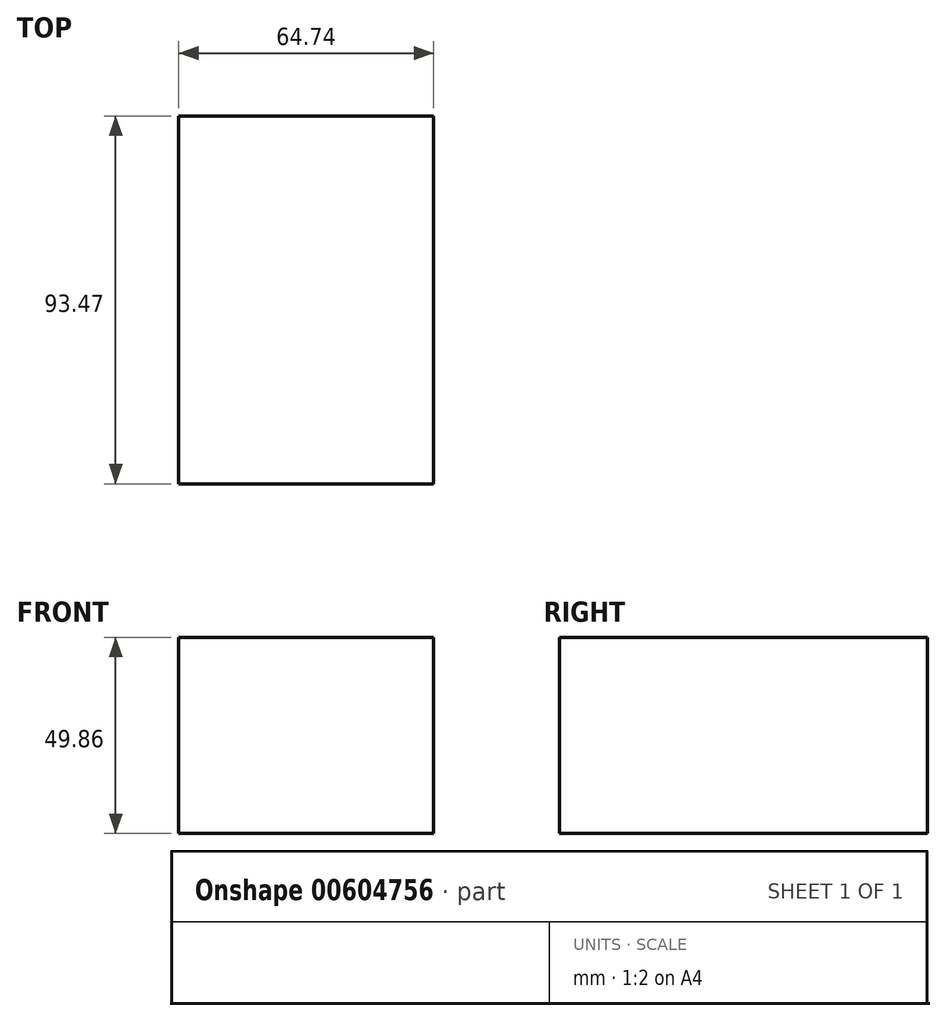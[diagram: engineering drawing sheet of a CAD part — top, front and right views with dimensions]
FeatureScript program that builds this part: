
annotation { "Feature Type Name" : "Feature", "Feature Type Description" : "" }
export const myFeature = defineFeature(function(context is Context, id is Id, definition is map)
    precondition{}
    {
        {
            var Q0;
            Q0=qCreatedBy(makeId("Front.planeOp"),FACE);
            var sketch = newSketch(context, id + "F0", { "sketchPlane" : qUnion([Q0])});
            skLineSegment(sketch, "E0.bottom", {"start": v(-31.2, 24.93) * mm, "end": v(33.54, 24.93) * mm});
            skLineSegment(sketch, "E0.top", {"start": v(-31.2, -24.93) * mm, "end": v(33.54, -24.93) * mm});
            skLineSegment(sketch, "E0.left", {"start": v(-31.2, 24.93) * mm, "end": v(-31.2, -24.93) * mm});
            skLineSegment(sketch, "E0.right", {"start": v(33.54, 24.93) * mm, "end": v(33.54, -24.93) * mm});
            skSolve(sketch);
        }
        {
            var Q0;
            Q0=makeQuery(id+"F0.imprint","IMPRINT",FACE,{"disambiguationData":[TD([[makeQuery(id+"F0.imprint","IMPRINT",EDGE,{"derivedFrom":sQuery(id+"F0.wireOp",EDGE,"E0.bottom")}),-1.0]])]});
            extrude(context, id + "F1", {"entities" : qUnion([Q0]), "depth" : 93.47 * mm, "offsetDistance" : 25.4 * mm});
        }
    });
